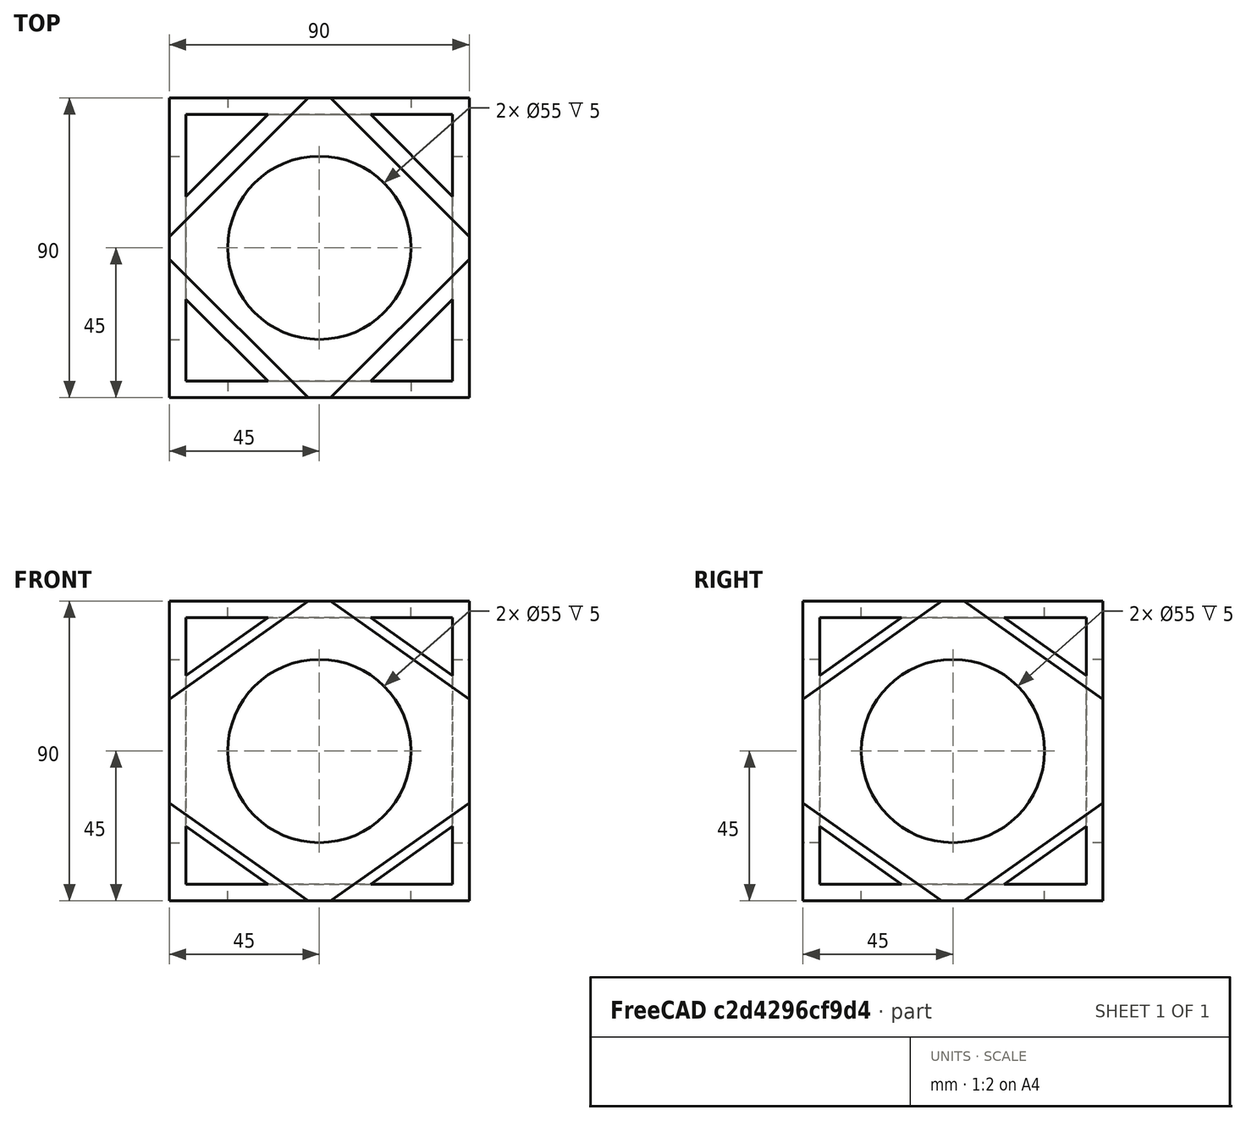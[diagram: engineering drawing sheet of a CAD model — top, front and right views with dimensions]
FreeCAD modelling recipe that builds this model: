
FCSTD DOCUMENT  (FreeCAD 0.17R13519 (Git))
Label: test003_whiffle
License: All rights reserved
LicenseURL: http://en.wikipedia.org/wiki/All_rights_reserved
objects: Part::Box×6, Part::Cut×5, Part::Cylinder×3, Part::MultiFuse×1
note: 15 computed .brp shape members not serialized (recipe doc carries the construction recipe); baked Part::Feature solids carry a one-line shape summary decoded from their .brp

FEATURE [Part::Box] Box  label="Cube"
  AttacherType = Attacher::AttachEngine3D
  Height = 90
  Length = 90
  Placement = pos=(-45,-45,-45) rot=(0,0,1;0rad)
  Width = 90
FEATURE [Part::Box] Box001  label="Cube001"
  AttacherType = Attacher::AttachEngine3D
  Height = 80
  Length = 80
  Placement = pos=(-40,-40,-40) rot=(0,0,1;0rad)
  Width = 80
FEATURE [Part::Cylinder] Cylinder
  Angle = 360
  AttacherType = Attacher::AttachEngine3D
  Height = 120
  Placement = pos=(0,0,-60) rot=(0,0,1;0rad)
  Radius = 27.5
FEATURE [Part::Cylinder] Cylinder001
  Angle = 360
  AttacherType = Attacher::AttachEngine3D
  Height = 120
  Placement = pos=(0,60,0) rot=(1,0,0;1.5708rad)
  Radius = 27.5
FEATURE [Part::Cylinder] Cylinder002
  Angle = 360
  AttacherType = Attacher::AttachEngine3D
  Height = 120
  Placement = pos=(-60,0,0) rot=(0,1,0;1.5708rad)
  Radius = 27.5
FEATURE [Part::MultiFuse] Fusion
  Shapes = -> [Box001,Cylinder,Cylinder001,Cylinder002]
FEATURE [Part::Cut] Cut
  Base = -> Box
  Tool = -> Fusion
FEATURE [Part::Box] Box002  label="Cube002"
  AttacherType = Attacher::AttachEngine3D
  Height = 112
  Length = 140
  Placement = pos=(-49.4975,-49.4975,-79.196) rot=(0.678598,0.281085,0.678598;1.09606rad)
  Width = 112
FEATURE [Part::Box] Box003  label="Cube003"
  AttacherType = Attacher::AttachEngine3D
  Height = 180
  Length = 180
  Placement = pos=(-63.6396,-63.6396,-127.279) rot=(0.678598,0.281085,0.678598;1.09606rad)
  Width = 180
FEATURE [Part::Box] Box004  label="Cube004"
  AttacherType = Attacher::AttachEngine3D
  Height = 112
  Length = 140
  Placement = pos=(-49.4975,49.4975,-79.196) rot=(-0.678598,0.281085,0.678598;5.18713rad)
  Width = 112
FEATURE [Part::Box] Box005  label="Cube005"
  AttacherType = Attacher::AttachEngine3D
  Height = 180
  Length = 180
  Placement = pos=(-63.6396,63.6396,-127.279) rot=(-0.678598,0.281085,0.678598;5.18713rad)
  Width = 180
FEATURE [Part::Cut] Cut001
  Base = -> Box003
  Tool = -> Box002
FEATURE [Part::Cut] Cut002
  Base = -> Box005
  Tool = -> Box004
FEATURE [Part::Cut] Cut003
  Base = -> Cut
  Tool = -> Cut001
FEATURE [Part::Cut] Cut004
  Base = -> Cut003
  Tool = -> Cut002
